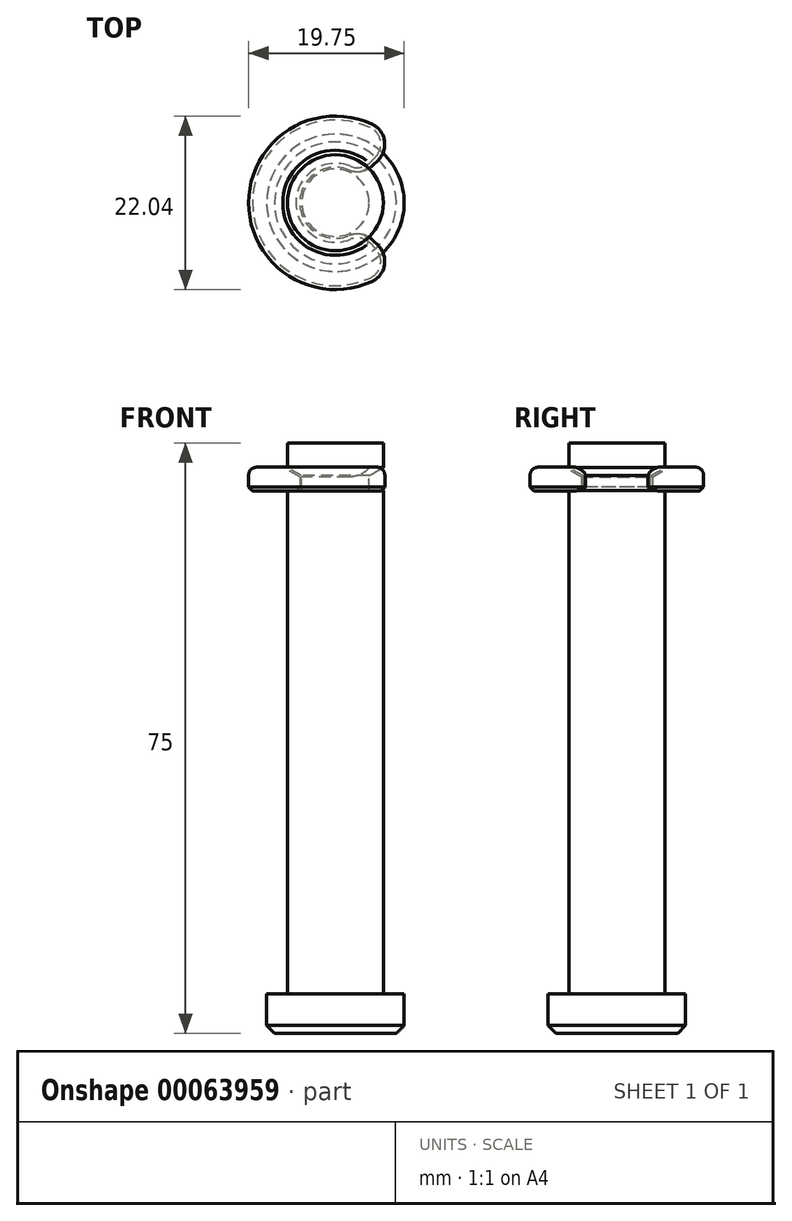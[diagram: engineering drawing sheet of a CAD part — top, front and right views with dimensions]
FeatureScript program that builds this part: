
annotation { "Feature Type Name" : "Feature", "Feature Type Description" : "" }
export const myFeature = defineFeature(function(context is Context, id is Id, definition is map)
    precondition{}
    {
        {
            var Q0;
            Q0=qCreatedBy(makeId("Top.planeOp"),FACE);
            var sketch = newSketch(context, id + "F0", { "sketchPlane" : qUnion([Q0])});
            skCircle(sketch, "E0", {"center": v(0, 0) * mm, "radius": 8.73 * mm});
            skSolve(sketch);
        }
        {
            var Q0;
            Q0 = qSketchRegion(id + "F0", true);
            extrude(context, id + "F1", {"entities" : qUnion([Q0]), "depth" : 5 * mm});
        }
        {
            var Q0;
            Q0=makeQuery(id+"F1.opExtrude","CAP_FACE",FACE,{"disambiguationData":[OSD([sQuery(id+"F0.wireOp",EDGE,"E0")])],"isStart":false});
            var sketch = newSketch(context, id + "F2", { "sketchPlane" : qUnion([Q0])});
            skCircle(sketch, "E1", {"center": v(0, 0) * mm, "radius": 6.1 * mm});
            skSolve(sketch);
        }
        {
            var Q0;
            Q0 = qSketchRegion(id + "F2", true);
            extrude(context, id + "F3", {"entities" : qUnion([Q0]), "operationType" : NewBodyOperationType.ADD, "depth" : 70 * mm});
        }
        {
            var Q0;
            Q0=qCreatedBy(makeId("Front.planeOp"),FACE);
            var sketch = newSketch(context, id + "F4", { "sketchPlane" : qUnion([Q0])});
            skLineSegment(sketch, "E2", {"start": v(-6.28, 69) * mm, "end": v(-4.28, 69) * mm});
            skLineSegment(sketch, "E3", {"start": v(-4.28, 69) * mm, "end": v(-4.28, 70.85) * mm});
            skLineSegment(sketch, "E4", {"start": v(-4.28, 70.85) * mm, "end": v(-6.28, 72) * mm});
            skLineSegment(sketch, "E5", {"start": v(-6.28, 72) * mm, "end": v(-6.28, 69) * mm});
            skSolve(sketch);
        }
        {
            var Q0;
            Q0 = qSketchRegion(id + "F4", true);
            var Q1;
            Q1=makeQuery(id+"F3.opExtrude","CAP_EDGE",EDGE,{"disambiguationData":[OSD([sQuery(id+"F2.wireOp",EDGE,"E1")])],"isStart":false});
            revolve(context, id + "F5", {"operationType" : NewBodyOperationType.REMOVE, "entities" : qUnion([Q0]), "axis" : qUnion([Q1]), "revolveType" : RevolveType.FULL, "oppositeDirection" : true});
        }
        {
            var Q0;
            Q0=makeQuery(id+"F1.opExtrude","CAP_EDGE",EDGE,{"disambiguationData":[OSD([sQuery(id+"F0.wireOp",EDGE,"E0")])],"isStart":true});
            chamfer(context, id + "F6", {"entities" : qUnion([Q0]), "width" : 1 * mm, "tangentPropagation" : true});
        }
        {
            var Q0;
            Q0=qCreatedBy(makeId("Front.planeOp"),FACE);
            var sketch = newSketch(context, id + "F7", { "sketchPlane" : qUnion([Q0])});
            skLineSegment(sketch, "E6", {"start": v(-11.02, 68.93) * mm, "end": v(-4.52, 68.93) * mm});
            skLineSegment(sketch, "E7", {"start": v(-4.52, 68.93) * mm, "end": v(-4.52, 70.69) * mm});
            skLineSegment(sketch, "E8", {"start": v(-4.52, 70.69) * mm, "end": v(-6.67, 71.93) * mm});
            skLineSegment(sketch, "E9", {"start": v(-6.67, 71.93) * mm, "end": v(-11.02, 71.93) * mm});
            skLineSegment(sketch, "E10", {"start": v(-11.02, 71.93) * mm, "end": v(-11.02, 68.93) * mm});
            skSolve(sketch);
        }
        {
            var Q0;
            Q0 = qSketchRegion(id + "F7", true);
            var Q1;
            Q1=makeQuery(id+"F3.opExtrude","CAP_EDGE",EDGE,{"disambiguationData":[OSD([sQuery(id+"F2.wireOp",EDGE,"E1")])],"isStart":false});
            revolve(context, id + "F8", {"entities" : qUnion([Q0]), "axis" : qUnion([Q1]), "revolveType" : RevolveType.SYMMETRIC, "angle" : 270 * degree});
        }
        {
            var Q0;
            Q0=makeQuery(id+"F8.opRevolve","CAP_EDGE",EDGE,{"disambiguationData":[OSD([sQuery(id+"F7.wireOp",EDGE,"E7")])],"isStart":true});
            var Q1;
            Q1=makeQuery(id+"F8.opRevolve","CAP_EDGE",EDGE,{"disambiguationData":[OSD([sQuery(id+"F7.wireOp",EDGE,"E7")])],"isStart":false});
            var Q2;
            Q2=makeQuery(id+"F8.opRevolve","CAP_EDGE",EDGE,{"disambiguationData":[OSD([sQuery(id+"F7.wireOp",EDGE,"E10")])],"isStart":true});
            var Q3;
            Q3=makeQuery(id+"F8.opRevolve","CAP_EDGE",EDGE,{"disambiguationData":[OSD([sQuery(id+"F7.wireOp",EDGE,"E10")])],"isStart":false});
            fillet(context, id + "F9", {"entities" : qUnion([Q0, Q1, Q2, Q3]), "radius" : 2.82 * mm, "tangentPropagation" : true, "allowEdgeOverflow" : false});
        }
        {
            var Q0;
            Q0=makeQuery(id+"F8.opRevolve","SWEPT_EDGE",EDGE,{"disambiguationData":[OSD([sQuery(id+"F7.wireOp",EDGE,"E6"),sQuery(id+"F7.wireOp",EDGE,"E10")])]});
            chamfer(context, id + "F10", {"entities" : qUnion([Q0]), "width" : .5 * mm, "tangentPropagation" : true});
        }
        {
            var Q0;
            Q0=makeQuery(id+"F9.opFillet","BLEND_EDGE",EDGE,{"blendedFrom":[makeQuery(id+"F8.opRevolve","CAP_EDGE",EDGE,{"disambiguationData":[OSD([sQuery(id+"F7.wireOp",EDGE,"E10")])],"isStart":false}),makeQuery(id+"F8.opRevolve","SWEPT_FACE",FACE,{"disambiguationData":[OSD([sQuery(id+"F7.wireOp",EDGE,"E9")])]})],"blendedInto":[makeQuery(id+"F8.opRevolve","SWEPT_FACE",FACE,{"disambiguationData":[OSD([sQuery(id+"F7.wireOp",EDGE,"E9")])]})]});
            fillet(context, id + "F11", {"entities" : qUnion([Q0]), "radius" : 1 * mm, "tangentPropagation" : true, "allowEdgeOverflow" : false});
        }
    });
